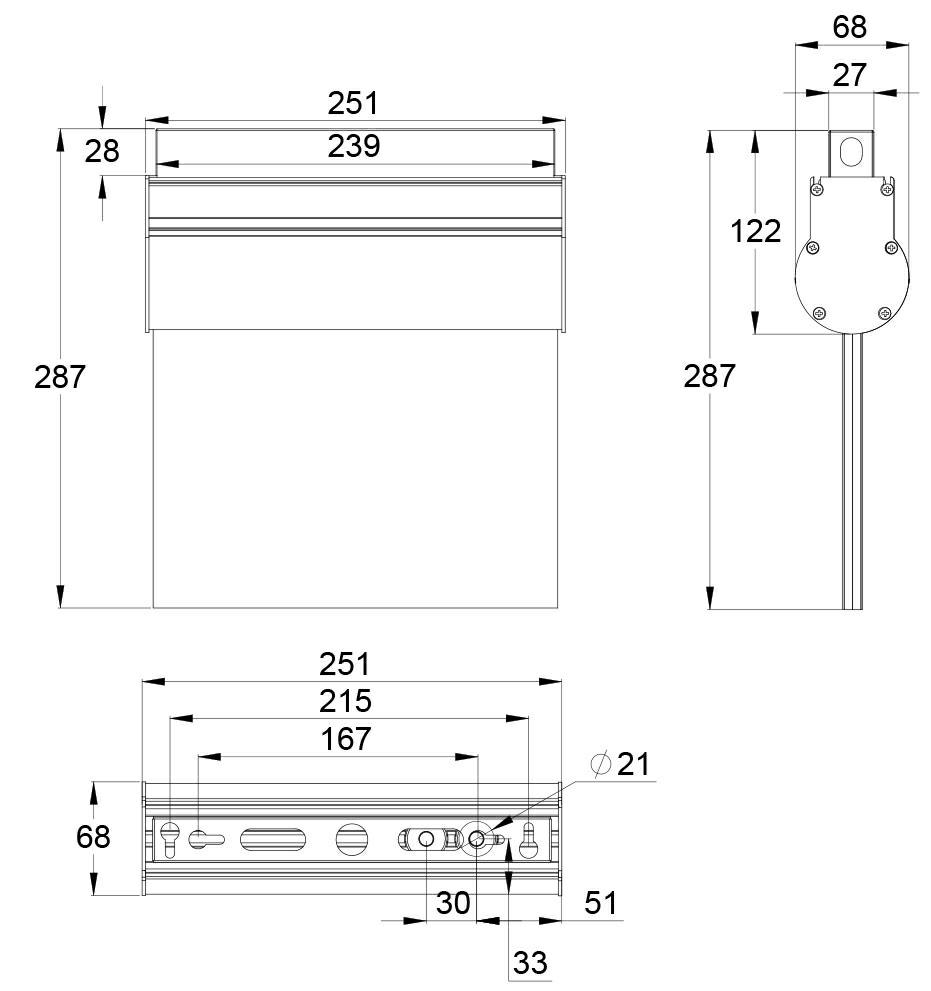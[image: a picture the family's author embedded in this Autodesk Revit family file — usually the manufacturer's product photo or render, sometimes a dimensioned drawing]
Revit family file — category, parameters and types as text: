
# Revit family: ESC 10 LED EMERGENCY EXIT LIGHT TW80251WK
name_source: partatom
category: Electrical Fixtures
revit_build: Autodesk Revit 2015 (Build: 20160512_0715(x64)
units: mm (PartAtom-declared; Revit-internal decimal feet)

## types (3) — shared parameters
Depth = 68 mm
Height = 298 mm  [stored 0.97769 ft]
Manufacturer = Teknoware Oy
Model = ESC 10 TW802
Product Code = TW80251WK
Viewing Distance = 40000 mm  [stored 131.234 ft]
Width = 324 mm  [stored 1.06299 ft]

## per-type parameters (varying)
| type | Back Pictogram | Down | Front Pictogram | Left | Right | Type Comments |
| -arrow right | Teknoware Pictogram PBV10401E left | No | Teknoware Pictogram PBV10401E right | No | Yes | PBV10401E |
| -arrow left | Teknoware Pictogram PBV10401E right | No | Teknoware Pictogram PBV10401E left | Yes | No | PBV10401E |
| -arrow down | Teknoware Pictogram PBV10402E | Yes | Teknoware Pictogram PBV10402E | No | No | PBV10402E |

note: [stored X ft] marks values corroborated as IEEE doubles in the binary element streams (Revit-internal decimal feet)

## geometry (parser evidence)
native form markers: Blend x8, Sweep x15
no freeform markers — native parametric forms only
